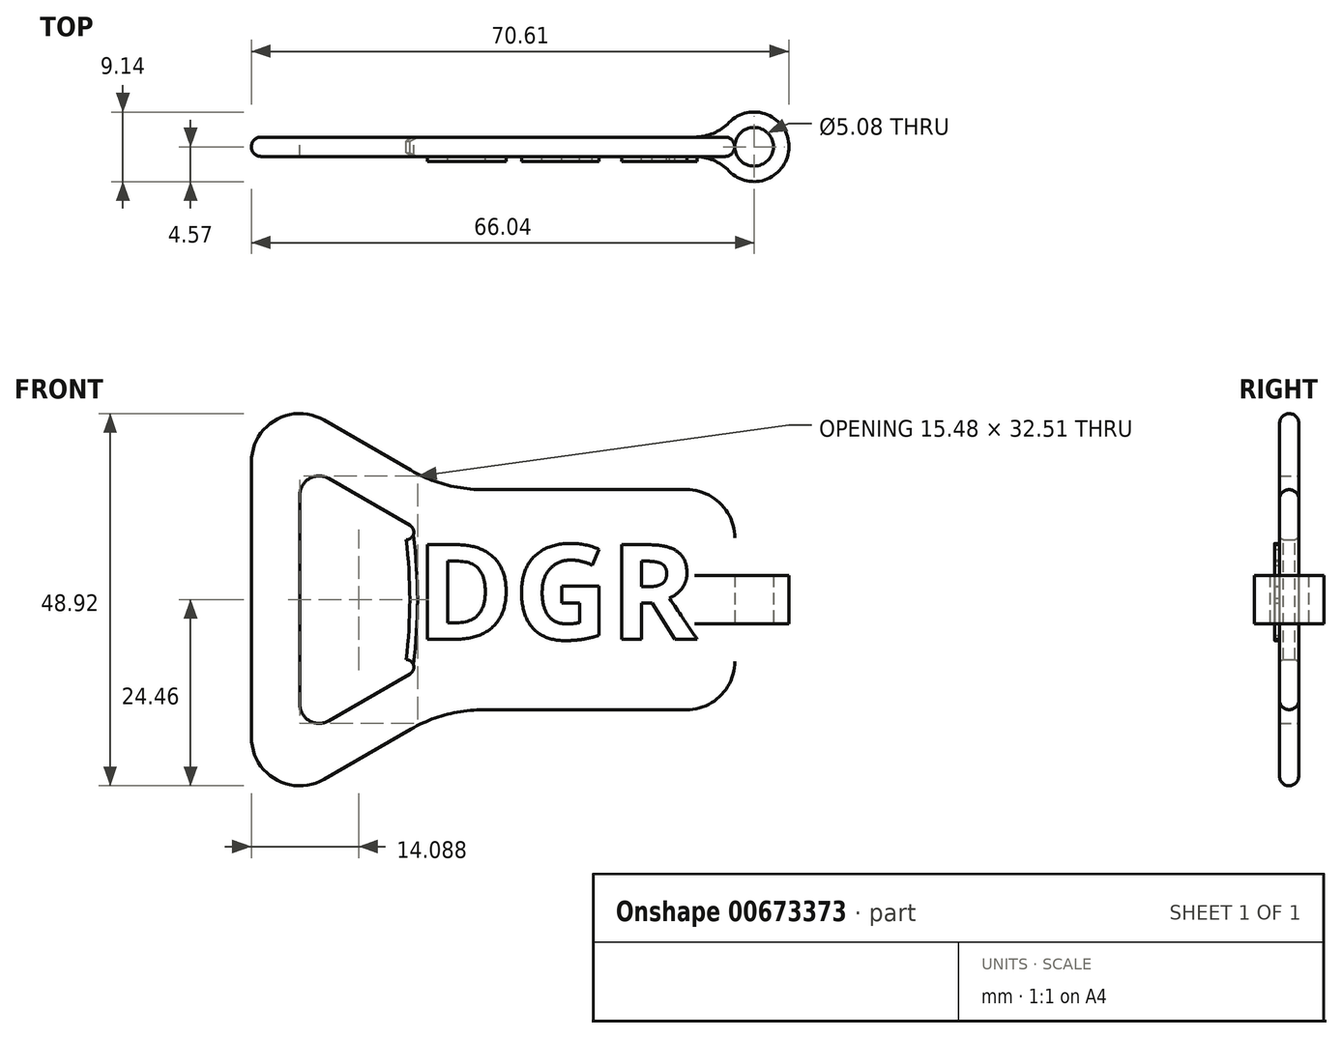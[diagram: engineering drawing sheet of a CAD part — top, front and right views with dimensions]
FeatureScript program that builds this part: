
annotation { "Feature Type Name" : "Feature", "Feature Type Description" : "" }
export const myFeature = defineFeature(function(context is Context, id is Id, definition is map)
    precondition{}
    {
        {
            var Q0;
            Q0=qCreatedBy(makeId("Front.planeOp"),FACE);
            var sketch = newSketch(context, id + "F0", { "sketchPlane" : qUnion([Q0])});
            skLineSegment(sketch, "E0", {"start": v(0, 0) * mm, "end": v(0, 8.11) * mm});
            skLineSegment(sketch, "E1", {"start": v(-6.35, 14.46) * mm, "end": v(-33, 14.46) * mm});
            skLineSegment(sketch, "E2", {"start": v(-42.51, 17) * mm, "end": v(-53.98, 23.61) * mm});
            skLineSegment(sketch, "E3", {"start": v(-63.5, 18.11) * mm, "end": v(-63.5, 0) * mm});
            skLineSegment(sketch, "E4", {"start": v(-63.5, 0) * mm, "end": v(0, 0) * mm});
            skLineSegment(sketch, "E5.0", {"start": v(-57.15, 13.72) * mm, "end": v(-57.15, 0) * mm});
            skLineSegment(sketch, "E5.1", {"start": v(-42.67, 9.77) * mm, "end": v(-53.34, 15.92) * mm});
            skPoint(sketch, "E6.visualSharp", {"position": v(0, 14.46) * mm});
            skArc(sketch, "E6.filletArc", {"start": v(0, 8.11) * mm, "mid": v(-1.86, 12.6) * mm, "end": v(-6.35, 14.46) * mm});
            skPoint(sketch, "E7.visualSharp", {"position": v(-63.5, 29.1) * mm});
            skArc(sketch, "E7.filletArc", {"start": v(-53.98, 23.61) * mm, "mid": v(-60.33, 23.6) * mm, "end": v(-63.5, 18.11) * mm});
            skArc(sketch, "E8.filletArc", {"start": v(-53.34, 15.92) * mm, "mid": v(-55.88, 15.92) * mm, "end": v(-57.15, 13.72) * mm});
            skArc(sketch, "E9.filletArc", {"start": v(-43.18, 7.87) * mm, "mid": v(-42.2, 8.63) * mm, "end": v(-42.67, 9.77) * mm});
            skPoint(sketch, "E10.visualSharp", {"position": v(-38.1, 14.46) * mm});
            skArc(sketch, "E10.filletArc", {"start": v(-42.51, 17) * mm, "mid": v(-37.93, 15.11) * mm, "end": v(-33, 14.46) * mm});
            skLineSegment(sketch, "E11.MirrorCS", {"start": v(0, 0) * mm, "end": v(0, -8.11) * mm});
            skArc(sketch, "E12.MirrorCS", {"start": v(0, -8.11) * mm, "mid": v(-1.86, -12.6) * mm, "end": v(-6.35, -14.46) * mm});
            skLineSegment(sketch, "E13.MirrorCS", {"start": v(-6.35, -14.46) * mm, "end": v(-33, -14.46) * mm});
            skArc(sketch, "E14.MirrorCS", {"start": v(-42.51, -17) * mm, "mid": v(-37.93, -15.11) * mm, "end": v(-33, -14.46) * mm});
            skLineSegment(sketch, "E15.MirrorCS", {"start": v(-42.51, -17) * mm, "end": v(-53.98, -23.61) * mm});
            skArc(sketch, "E16.MirrorCS", {"start": v(-53.98, -23.61) * mm, "mid": v(-60.33, -23.6) * mm, "end": v(-63.5, -18.11) * mm});
            skLineSegment(sketch, "E17.MirrorCS", {"start": v(-63.5, -18.11) * mm, "end": v(-63.5, 0) * mm});
            skLineSegment(sketch, "E18.MirrorCS", {"start": v(-57.15, -13.72) * mm, "end": v(-57.15, 0) * mm});
            skArc(sketch, "E19.MirrorCS", {"start": v(-53.34, -15.92) * mm, "mid": v(-55.88, -15.92) * mm, "end": v(-57.15, -13.72) * mm});
            skLineSegment(sketch, "E20.MirrorCS", {"start": v(-42.67, -9.77) * mm, "end": v(-53.34, -15.92) * mm});
            skArc(sketch, "E21.MirrorCS", {"start": v(-43.18, -7.87) * mm, "mid": v(-42.2, -8.63) * mm, "end": v(-42.67, -9.77) * mm});
            skArc(sketch, "E22", {"start": v(-43.18, -7.87) * mm, "mid": v(-42.69, 0) * mm, "end": v(-43.18, 7.87) * mm});
            skSolve(sketch);
        }
        {
            var Q0;
            Q0 = qSketchRegion(id + "F0", true);
            extrude(context, id + "F1", {"entities" : qUnion([Q0]), "depth" : 2.54 * mm, "offsetDistance" : 25.4 * mm});
        }
        {
            var Q0;
            Q0=makeQuery(id+"F1.opExtrude","CAP_EDGE",EDGE,{"disambiguationData":[OSD([sQuery(id+"F0.wireOp",EDGE,"E22")])],"isStart":false});
            var Q1;
            Q1=makeQuery(id+"F1.opExtrude","CAP_EDGE",EDGE,{"disambiguationData":[OSD([sQuery(id+"F0.wireOp",EDGE,"E22")])],"isStart":true});
            chamfer(context, id + "F2", {"entities" : qUnion([Q0, Q1]), "chamferType" : ChamferType.TWO_OFFSETS, "width1" : 0.5 * mm, "oppositeDirection" : false, "width2" : 1.02 * mm, "tangentPropagation" : true});
        }
        {
            var Q0;
            Q0=qCreatedBy(makeId("Top.planeOp"),FACE);
            var sketch = newSketch(context, id + "F3", { "sketchPlane" : qUnion([Q0])});
            skCircle(sketch, "E23", {"center": v(2.54, -1.27) * mm, "radius": 2.54 * mm});
            skCircle(sketch, "E24.0", {"center": v(2.54, -1.27) * mm, "radius": 4.57 * mm});
            skSolve(sketch);
        }
        {
            var Q0;
            Q0=makeQuery(id+"F3.imprint","IMPRINT",FACE,{"disambiguationData":[TD([[makeQuery(id+"F3.imprint","IMPRINT",EDGE,{"derivedFrom":sQuery(id+"F3.wireOp",EDGE,"E23")}),-1.0]])]});
            extrude(context, id + "F4", {"entities" : qUnion([Q0]), "operationType" : NewBodyOperationType.ADD, "endBound" : BoundingType.SYMMETRIC, "depth" : 6.35 * mm, "offsetDistance" : 25.4 * mm});
        }
        {
            var Q0;
            Q0=makeQuery(id+"F4.boolean.opBoolean","INTERSECT",EDGE,{"derivedFrom":[makeQuery(id+"F1.opExtrude","CAP_FACE",FACE,{"disambiguationData":[OSD([sQuery(id+"F0.wireOp",EDGE,"E0"),sQuery(id+"F0.wireOp",EDGE,"E1"),sQuery(id+"F0.wireOp",EDGE,"E2"),sQuery(id+"F0.wireOp",EDGE,"E3"),sQuery(id+"F0.wireOp",EDGE,"E5.0"),sQuery(id+"F0.wireOp",EDGE,"E5.1"),sQuery(id+"F0.wireOp",EDGE,"E6.filletArc"),sQuery(id+"F0.wireOp",EDGE,"E7.filletArc"),sQuery(id+"F0.wireOp",EDGE,"E8.filletArc"),sQuery(id+"F0.wireOp",EDGE,"E9.filletArc"),sQuery(id+"F0.wireOp",EDGE,"E10.filletArc"),sQuery(id+"F0.wireOp",EDGE,"E11.MirrorCS"),sQuery(id+"F0.wireOp",EDGE,"E12.MirrorCS"),sQuery(id+"F0.wireOp",EDGE,"E13.MirrorCS"),sQuery(id+"F0.wireOp",EDGE,"E14.MirrorCS"),sQuery(id+"F0.wireOp",EDGE,"E15.MirrorCS"),sQuery(id+"F0.wireOp",EDGE,"E16.MirrorCS"),sQuery(id+"F0.wireOp",EDGE,"E17.MirrorCS"),sQuery(id+"F0.wireOp",EDGE,"E18.MirrorCS"),sQuery(id+"F0.wireOp",EDGE,"E19.MirrorCS"),sQuery(id+"F0.wireOp",EDGE,"E20.MirrorCS"),sQuery(id+"F0.wireOp",EDGE,"E21.MirrorCS"),sQuery(id+"F0.wireOp",EDGE,"E22")])],"isStart":false}),makeQuery(id+"F4.opExtrude","SWEPT_FACE",FACE,{"disambiguationData":[OSD([sQuery(id+"F3.wireOp",EDGE,"E24.0")])]})]});
            var Q1;
            Q1=makeQuery(id+"F4.boolean.opBoolean","INTERSECT",EDGE,{"derivedFrom":[makeQuery(id+"F1.opExtrude","CAP_FACE",FACE,{"disambiguationData":[OSD([sQuery(id+"F0.wireOp",EDGE,"E0"),sQuery(id+"F0.wireOp",EDGE,"E1"),sQuery(id+"F0.wireOp",EDGE,"E2"),sQuery(id+"F0.wireOp",EDGE,"E3"),sQuery(id+"F0.wireOp",EDGE,"E5.0"),sQuery(id+"F0.wireOp",EDGE,"E5.1"),sQuery(id+"F0.wireOp",EDGE,"E6.filletArc"),sQuery(id+"F0.wireOp",EDGE,"E7.filletArc"),sQuery(id+"F0.wireOp",EDGE,"E8.filletArc"),sQuery(id+"F0.wireOp",EDGE,"E9.filletArc"),sQuery(id+"F0.wireOp",EDGE,"E10.filletArc"),sQuery(id+"F0.wireOp",EDGE,"E11.MirrorCS"),sQuery(id+"F0.wireOp",EDGE,"E12.MirrorCS"),sQuery(id+"F0.wireOp",EDGE,"E13.MirrorCS"),sQuery(id+"F0.wireOp",EDGE,"E14.MirrorCS"),sQuery(id+"F0.wireOp",EDGE,"E15.MirrorCS"),sQuery(id+"F0.wireOp",EDGE,"E16.MirrorCS"),sQuery(id+"F0.wireOp",EDGE,"E17.MirrorCS"),sQuery(id+"F0.wireOp",EDGE,"E18.MirrorCS"),sQuery(id+"F0.wireOp",EDGE,"E19.MirrorCS"),sQuery(id+"F0.wireOp",EDGE,"E20.MirrorCS"),sQuery(id+"F0.wireOp",EDGE,"E21.MirrorCS"),sQuery(id+"F0.wireOp",EDGE,"E22")])],"isStart":true}),makeQuery(id+"F4.opExtrude","SWEPT_FACE",FACE,{"disambiguationData":[OSD([sQuery(id+"F3.wireOp",EDGE,"E24.0")])]})]});
            fillet(context, id + "F5", {"entities" : qUnion([Q0, Q1]), "radius" : 6.35 * mm, "tangentPropagation" : true, "allowEdgeOverflow" : false});
        }
        {
            var Q0;
            Q0=qCreatedBy(makeId("Front.planeOp"),FACE);
            var sketch = newSketch(context, id + "F6", { "sketchPlane" : qUnion([Q0])});
            skText(sketch, "E25", { "text": "DGR", "fontName": "OpenSans-Bold.ttf"});
            const initialGuessF6  = {"E25": [-0.04191, -0.00521, 1, 0, 0.01253]};
            skSetInitialGuess(sketch, initialGuessF6);
            skSolve(sketch);
        }
        {
            var Q0;
            Q0 = qSketchRegion(id + "F6", true);
            extrude(context, id + "F7", {"entities" : qUnion([Q0]), "operationType" : NewBodyOperationType.ADD, "depth" : 3.17 * mm, "offsetDistance" : 25.4 * mm});
        }
        {
            var Q0;
            Q0=makeQuery(id+"F1.opExtrude","CAP_EDGE",EDGE,{"disambiguationData":[OSD([sQuery(id+"F0.wireOp",EDGE,"E1")])],"isStart":false});
            var Q1;
            Q1=makeQuery(id+"F1.opExtrude","CAP_EDGE",EDGE,{"disambiguationData":[OSD([sQuery(id+"F0.wireOp",EDGE,"E13.MirrorCS")])],"isStart":true});
            fillet(context, id + "F8", {"entities" : qUnion([Q0, Q1]), "radius" : 1.27 * mm, "tangentPropagation" : true, "allowEdgeOverflow" : false});
        }
    });
